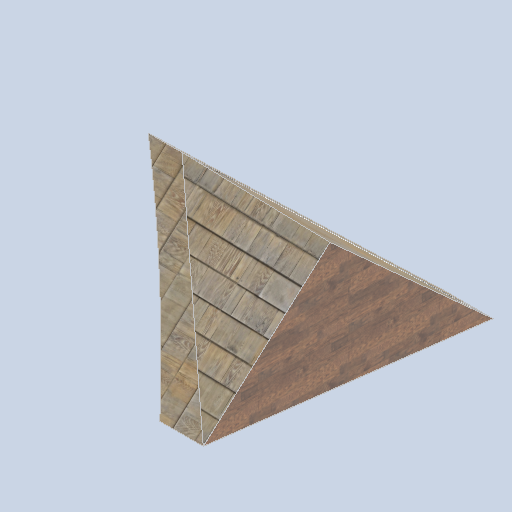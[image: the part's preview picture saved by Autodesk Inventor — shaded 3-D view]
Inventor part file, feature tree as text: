
AUTODESK INVENTOR PART (.ipt)
format: ipt  version: 2024.2 (Build 282272000, 272)  size: 288,256 bytes
history: native  units: in
note: dims shown in document units (in); Inventor stores cm internally (conversion verified against a paired STEP export)
features: sketch x7, plane x6, other x3
ambient origin geometry x8: Origin, YZ Plane, XZ Plane, XY Plane, X Axis, Y Axis, Z Axis, Center Point
bodies: Solid1 (feature_tree)
feature tree (16):
  other  "panel_pad_02 .ipt"
  other  "Solid1::panel_pad_02 .ipt"
  other  "TaggingFeature1"
  sketch  "Sketch1"  dims[d0=0.3937in]
  sketch  "Sketch2"
  sketch  "Sketch3"
  sketch  "Sketch6"
  sketch  "Sketch7"
  sketch  "Sketch8"
  sketch  "Sketch9"
  plane  "Work Plane1"
  plane  "Work Plane2"
  plane  "Work Plane3"
  plane  "Work Plane4"
  plane  "Work Plane5"
  plane  "Work Plane6"
